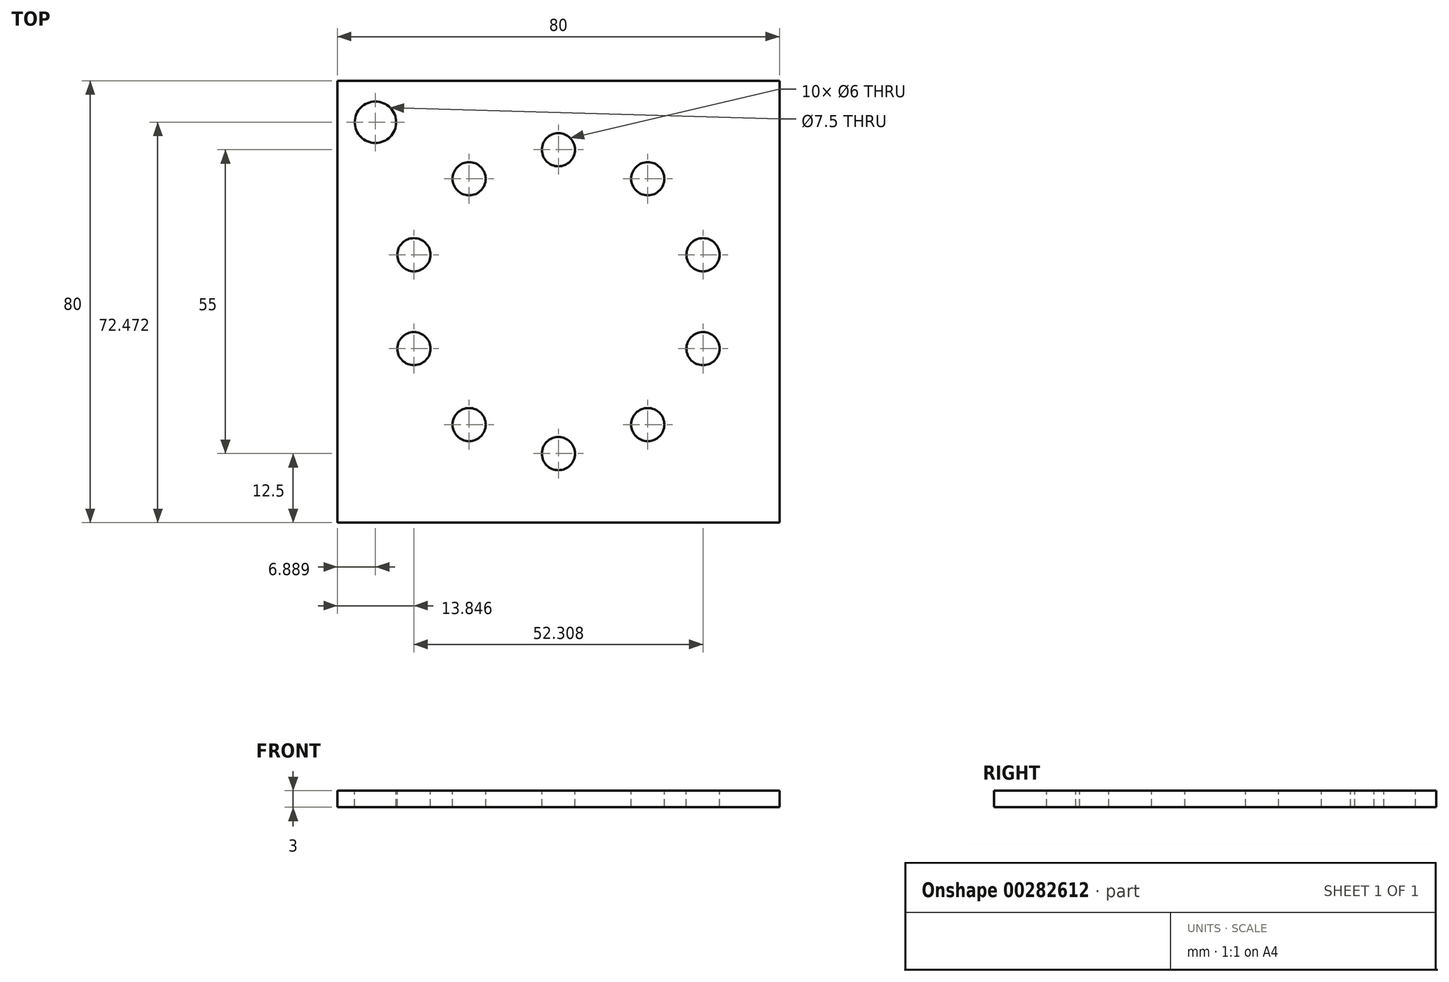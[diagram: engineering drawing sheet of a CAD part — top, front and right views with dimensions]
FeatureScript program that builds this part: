
annotation { "Feature Type Name" : "Feature", "Feature Type Description" : "" }
export const myFeature = defineFeature(function(context is Context, id is Id, definition is map)
    precondition{}
    {
        {
            var Q0;
            Q0=qCreatedBy(makeId("Top.planeOp"),FACE);
            var sketch = newSketch(context, id + "F0", { "sketchPlane" : qUnion([Q0])});
            skLineSegment(sketch, "E0.bottom", {"start": v(-40, 40) * mm, "end": v(40, 40) * mm});
            skLineSegment(sketch, "E0.top", {"start": v(-40, -40) * mm, "end": v(40, -40) * mm});
            skLineSegment(sketch, "E0.left", {"start": v(-40, 40) * mm, "end": v(-40, -40) * mm});
            skLineSegment(sketch, "E0.right", {"start": v(40, 40) * mm, "end": v(40, -40) * mm});
            skPoint(sketch, "E0.middle", {"position": v(0, 0) * mm});
            skSolve(sketch);
        }
        {
            var Q0;
            Q0=makeQuery(id+"F0.imprint","IMPRINT",FACE,{"disambiguationData":[TD([[makeQuery(id+"F0.imprint","IMPRINT",EDGE,{"derivedFrom":sQuery(id+"F0.wireOp",EDGE,"E0.bottom")}),-1.0]])]});
            extrude(context, id + "F1", {"entities" : qUnion([Q0]), "depth" : 3 * mm});
        }
        {
            var Q0;
            Q0=makeQuery(id+"F1.opExtrude","CAP_FACE",FACE,{"disambiguationData":[OSD([sQuery(id+"F0.wireOp",EDGE,"E0.bottom"),sQuery(id+"F0.wireOp",EDGE,"E0.top"),sQuery(id+"F0.wireOp",EDGE,"E0.left"),sQuery(id+"F0.wireOp",EDGE,"E0.right")])],"isStart":false});
            var sketch = newSketch(context, id + "F2", { "sketchPlane" : qUnion([Q0])});
            skCircle(sketch, "E1", {"center": v(0, 0) * mm, "radius": 35 * mm});
            skCircle(sketch, "E2", {"center": v(0, 0) * mm, "radius": 27.5 * mm});
            skCircle(sketch, "E3", {"center": v(0, 27.5) * mm, "radius": 3 * mm});
            skCircle(sketch, "E4.1.0", {"center": v(-16.16, 22.25) * mm, "radius": 3 * mm});
            skCircle(sketch, "E4.2.0", {"center": v(-26.15, 8.5) * mm, "radius": 3 * mm});
            skCircle(sketch, "E4.3.0", {"center": v(-26.15, -8.5) * mm, "radius": 3 * mm});
            skCircle(sketch, "E4.4.0", {"center": v(-16.16, -22.25) * mm, "radius": 3 * mm});
            skCircle(sketch, "E4.5.0", {"center": v(0, -27.5) * mm, "radius": 3 * mm});
            skCircle(sketch, "E4.6.0", {"center": v(16.16, -22.25) * mm, "radius": 3 * mm});
            skCircle(sketch, "E4.7.0", {"center": v(26.15, -8.5) * mm, "radius": 3 * mm});
            skCircle(sketch, "E4.8.0", {"center": v(26.15, 8.5) * mm, "radius": 3 * mm});
            skCircle(sketch, "E4.9.0", {"center": v(16.16, 22.25) * mm, "radius": 3 * mm});
            skSolve(sketch);
        }
        {
            var Q0;
            {var subQ0=sQuery(id+"F2.wireOp",EDGE,"E4.1.0");var subQ1=sQuery(id+"F2.wireOp",EDGE,"E2");var subQ2=makeQuery(id+"F2.imprint","INTERSECT",VERTEX,{"disambiguationData":[OD(0.0)],"derivedFrom":[subQ1,subQ0]});Q0=makeQuery(id+"F2.imprint","IMPRINT",FACE,{"disambiguationData":[TD([[makeQuery(id+"F2.imprint","IMPRINT",EDGE,{"disambiguationData":[TD([[subQ2,-1.0]])],"derivedFrom":subQ1}),1.0]])]});}
            var Q1;
            {var subQ0=sQuery(id+"F2.wireOp",EDGE,"E4.1.0");var subQ1=sQuery(id+"F2.wireOp",EDGE,"E2");var subQ2=makeQuery(id+"F2.imprint","INTERSECT",VERTEX,{"disambiguationData":[OD(0.0)],"derivedFrom":[subQ1,subQ0]});Q1=makeQuery(id+"F2.imprint","IMPRINT",FACE,{"disambiguationData":[TD([[makeQuery(id+"F2.imprint","IMPRINT",EDGE,{"disambiguationData":[TD([[subQ2,-1.0]])],"derivedFrom":subQ1}),-1.0]])]});}
            var Q2;
            {var subQ0=sQuery(id+"F2.wireOp",EDGE,"E3");var subQ1=sQuery(id+"F2.wireOp",EDGE,"E2");var subQ2=makeQuery(id+"F2.imprint","INTERSECT",VERTEX,{"disambiguationData":[OD(0.0)],"derivedFrom":[subQ1,subQ0]});Q2=makeQuery(id+"F2.imprint","IMPRINT",FACE,{"disambiguationData":[TD([[makeQuery(id+"F2.imprint","IMPRINT",EDGE,{"disambiguationData":[TD([[subQ2,-1.0]])],"derivedFrom":subQ1}),1.0]])]});}
            var Q3;
            {var subQ0=sQuery(id+"F2.wireOp",EDGE,"E3");var subQ1=sQuery(id+"F2.wireOp",EDGE,"E2");var subQ2=makeQuery(id+"F2.imprint","INTERSECT",VERTEX,{"disambiguationData":[OD(0.0)],"derivedFrom":[subQ1,subQ0]});Q3=makeQuery(id+"F2.imprint","IMPRINT",FACE,{"disambiguationData":[TD([[makeQuery(id+"F2.imprint","IMPRINT",EDGE,{"disambiguationData":[TD([[subQ2,-1.0]])],"derivedFrom":subQ1}),-1.0]])]});}
            var Q4;
            {var subQ0=sQuery(id+"F2.wireOp",EDGE,"E4.9.0");var subQ1=sQuery(id+"F2.wireOp",EDGE,"E2");var subQ2=makeQuery(id+"F2.imprint","INTERSECT",VERTEX,{"disambiguationData":[OD(0.0)],"derivedFrom":[subQ1,subQ0]});Q4=makeQuery(id+"F2.imprint","IMPRINT",FACE,{"disambiguationData":[TD([[makeQuery(id+"F2.imprint","IMPRINT",EDGE,{"disambiguationData":[TD([[subQ2,-1.0]])],"derivedFrom":subQ1}),1.0]])]});}
            var Q5;
            {var subQ0=sQuery(id+"F2.wireOp",EDGE,"E4.9.0");var subQ1=sQuery(id+"F2.wireOp",EDGE,"E2");var subQ2=makeQuery(id+"F2.imprint","INTERSECT",VERTEX,{"disambiguationData":[OD(0.0)],"derivedFrom":[subQ1,subQ0]});Q5=makeQuery(id+"F2.imprint","IMPRINT",FACE,{"disambiguationData":[TD([[makeQuery(id+"F2.imprint","IMPRINT",EDGE,{"disambiguationData":[TD([[subQ2,-1.0]])],"derivedFrom":subQ1}),-1.0]])]});}
            var Q6;
            {var subQ0=sQuery(id+"F2.wireOp",EDGE,"E4.8.0");var subQ1=sQuery(id+"F2.wireOp",EDGE,"E2");var subQ2=makeQuery(id+"F2.imprint","INTERSECT",VERTEX,{"disambiguationData":[OD(0.0)],"derivedFrom":[subQ1,subQ0]});Q6=makeQuery(id+"F2.imprint","IMPRINT",FACE,{"disambiguationData":[TD([[makeQuery(id+"F2.imprint","IMPRINT",EDGE,{"disambiguationData":[TD([[subQ2,1.0]])],"derivedFrom":subQ1}),-1.0]])]});}
            var Q7;
            {var subQ0=sQuery(id+"F2.wireOp",EDGE,"E4.8.0");var subQ1=sQuery(id+"F2.wireOp",EDGE,"E2");var subQ2=makeQuery(id+"F2.imprint","INTERSECT",VERTEX,{"disambiguationData":[OD(0.0)],"derivedFrom":[subQ1,subQ0]});Q7=makeQuery(id+"F2.imprint","IMPRINT",FACE,{"disambiguationData":[TD([[makeQuery(id+"F2.imprint","IMPRINT",EDGE,{"disambiguationData":[TD([[subQ2,1.0]])],"derivedFrom":subQ1}),1.0]])]});}
            var Q8;
            {var subQ0=sQuery(id+"F2.wireOp",EDGE,"E4.7.0");var subQ1=sQuery(id+"F2.wireOp",EDGE,"E2");var subQ2=makeQuery(id+"F2.imprint","INTERSECT",VERTEX,{"disambiguationData":[OD(0.0)],"derivedFrom":[subQ1,subQ0]});Q8=makeQuery(id+"F2.imprint","IMPRINT",FACE,{"disambiguationData":[TD([[makeQuery(id+"F2.imprint","IMPRINT",EDGE,{"disambiguationData":[TD([[subQ2,-1.0]])],"derivedFrom":subQ1}),-1.0]])]});}
            var Q9;
            {var subQ0=sQuery(id+"F2.wireOp",EDGE,"E4.7.0");var subQ1=sQuery(id+"F2.wireOp",EDGE,"E2");var subQ2=makeQuery(id+"F2.imprint","INTERSECT",VERTEX,{"disambiguationData":[OD(0.0)],"derivedFrom":[subQ1,subQ0]});Q9=makeQuery(id+"F2.imprint","IMPRINT",FACE,{"disambiguationData":[TD([[makeQuery(id+"F2.imprint","IMPRINT",EDGE,{"disambiguationData":[TD([[subQ2,-1.0]])],"derivedFrom":subQ1}),1.0]])]});}
            var Q10;
            {var subQ0=sQuery(id+"F2.wireOp",EDGE,"E4.6.0");var subQ1=sQuery(id+"F2.wireOp",EDGE,"E2");var subQ2=makeQuery(id+"F2.imprint","INTERSECT",VERTEX,{"disambiguationData":[OD(0.0)],"derivedFrom":[subQ1,subQ0]});Q10=makeQuery(id+"F2.imprint","IMPRINT",FACE,{"disambiguationData":[TD([[makeQuery(id+"F2.imprint","IMPRINT",EDGE,{"disambiguationData":[TD([[subQ2,-1.0]])],"derivedFrom":subQ1}),-1.0]])]});}
            var Q11;
            {var subQ0=sQuery(id+"F2.wireOp",EDGE,"E4.6.0");var subQ1=sQuery(id+"F2.wireOp",EDGE,"E2");var subQ2=makeQuery(id+"F2.imprint","INTERSECT",VERTEX,{"disambiguationData":[OD(0.0)],"derivedFrom":[subQ1,subQ0]});Q11=makeQuery(id+"F2.imprint","IMPRINT",FACE,{"disambiguationData":[TD([[makeQuery(id+"F2.imprint","IMPRINT",EDGE,{"disambiguationData":[TD([[subQ2,-1.0]])],"derivedFrom":subQ1}),1.0]])]});}
            var Q12;
            {var subQ0=sQuery(id+"F2.wireOp",EDGE,"E4.5.0");var subQ1=sQuery(id+"F2.wireOp",EDGE,"E2");var subQ2=makeQuery(id+"F2.imprint","INTERSECT",VERTEX,{"disambiguationData":[OD(0.0)],"derivedFrom":[subQ1,subQ0]});Q12=makeQuery(id+"F2.imprint","IMPRINT",FACE,{"disambiguationData":[TD([[makeQuery(id+"F2.imprint","IMPRINT",EDGE,{"disambiguationData":[TD([[subQ2,-1.0]])],"derivedFrom":subQ1}),1.0]])]});}
            var Q13;
            {var subQ0=sQuery(id+"F2.wireOp",EDGE,"E4.5.0");var subQ1=sQuery(id+"F2.wireOp",EDGE,"E2");var subQ2=makeQuery(id+"F2.imprint","INTERSECT",VERTEX,{"disambiguationData":[OD(0.0)],"derivedFrom":[subQ1,subQ0]});Q13=makeQuery(id+"F2.imprint","IMPRINT",FACE,{"disambiguationData":[TD([[makeQuery(id+"F2.imprint","IMPRINT",EDGE,{"disambiguationData":[TD([[subQ2,-1.0]])],"derivedFrom":subQ1}),-1.0]])]});}
            var Q14;
            {var subQ0=sQuery(id+"F2.wireOp",EDGE,"E4.4.0");var subQ1=sQuery(id+"F2.wireOp",EDGE,"E2");var subQ2=makeQuery(id+"F2.imprint","INTERSECT",VERTEX,{"disambiguationData":[OD(0.0)],"derivedFrom":[subQ1,subQ0]});Q14=makeQuery(id+"F2.imprint","IMPRINT",FACE,{"disambiguationData":[TD([[makeQuery(id+"F2.imprint","IMPRINT",EDGE,{"disambiguationData":[TD([[subQ2,-1.0]])],"derivedFrom":subQ1}),-1.0]])]});}
            var Q15;
            {var subQ0=sQuery(id+"F2.wireOp",EDGE,"E4.4.0");var subQ1=sQuery(id+"F2.wireOp",EDGE,"E2");var subQ2=makeQuery(id+"F2.imprint","INTERSECT",VERTEX,{"disambiguationData":[OD(0.0)],"derivedFrom":[subQ1,subQ0]});Q15=makeQuery(id+"F2.imprint","IMPRINT",FACE,{"disambiguationData":[TD([[makeQuery(id+"F2.imprint","IMPRINT",EDGE,{"disambiguationData":[TD([[subQ2,-1.0]])],"derivedFrom":subQ1}),1.0]])]});}
            var Q16;
            {var subQ0=sQuery(id+"F2.wireOp",EDGE,"E4.3.0");var subQ1=sQuery(id+"F2.wireOp",EDGE,"E2");var subQ2=makeQuery(id+"F2.imprint","INTERSECT",VERTEX,{"disambiguationData":[OD(0.0)],"derivedFrom":[subQ1,subQ0]});Q16=makeQuery(id+"F2.imprint","IMPRINT",FACE,{"disambiguationData":[TD([[makeQuery(id+"F2.imprint","IMPRINT",EDGE,{"disambiguationData":[TD([[subQ2,-1.0]])],"derivedFrom":subQ1}),1.0]])]});}
            var Q17;
            {var subQ0=sQuery(id+"F2.wireOp",EDGE,"E4.3.0");var subQ1=sQuery(id+"F2.wireOp",EDGE,"E2");var subQ2=makeQuery(id+"F2.imprint","INTERSECT",VERTEX,{"disambiguationData":[OD(0.0)],"derivedFrom":[subQ1,subQ0]});Q17=makeQuery(id+"F2.imprint","IMPRINT",FACE,{"disambiguationData":[TD([[makeQuery(id+"F2.imprint","IMPRINT",EDGE,{"disambiguationData":[TD([[subQ2,-1.0]])],"derivedFrom":subQ1}),-1.0]])]});}
            var Q18;
            {var subQ0=sQuery(id+"F2.wireOp",EDGE,"E4.2.0");var subQ1=sQuery(id+"F2.wireOp",EDGE,"E2");var subQ2=makeQuery(id+"F2.imprint","INTERSECT",VERTEX,{"disambiguationData":[OD(0.0)],"derivedFrom":[subQ1,subQ0]});Q18=makeQuery(id+"F2.imprint","IMPRINT",FACE,{"disambiguationData":[TD([[makeQuery(id+"F2.imprint","IMPRINT",EDGE,{"disambiguationData":[TD([[subQ2,-1.0]])],"derivedFrom":subQ1}),1.0]])]});}
            var Q19;
            {var subQ0=sQuery(id+"F2.wireOp",EDGE,"E4.2.0");var subQ1=sQuery(id+"F2.wireOp",EDGE,"E2");var subQ2=makeQuery(id+"F2.imprint","INTERSECT",VERTEX,{"disambiguationData":[OD(0.0)],"derivedFrom":[subQ1,subQ0]});Q19=makeQuery(id+"F2.imprint","IMPRINT",FACE,{"disambiguationData":[TD([[makeQuery(id+"F2.imprint","IMPRINT",EDGE,{"disambiguationData":[TD([[subQ2,-1.0]])],"derivedFrom":subQ1}),-1.0]])]});}
            extrude(context, id + "F3", {"entities" : qUnion([Q0, Q1, Q2, Q3, Q4, Q5, Q6, Q7, Q8, Q9, Q10, Q11, Q12, Q13, Q14, Q15, Q16, Q17, Q18, Q19]), "operationType" : NewBodyOperationType.REMOVE, "oppositeDirection" : true, "depth" : 25 * mm});
        }
        {
            var Q0;
            Q0=makeQuery(id+"F1.opExtrude","CAP_FACE",FACE,{"disambiguationData":[OSD([sQuery(id+"F0.wireOp",EDGE,"E0.bottom"),sQuery(id+"F0.wireOp",EDGE,"E0.top"),sQuery(id+"F0.wireOp",EDGE,"E0.left"),sQuery(id+"F0.wireOp",EDGE,"E0.right")])],"isStart":false});
            var sketch = newSketch(context, id + "F4", { "sketchPlane" : qUnion([Q0])});
            skCircle(sketch, "E5", {"center": v(-33.11, 32.47) * mm, "radius": 3.75 * mm});
            skSolve(sketch);
        }
        {
            var Q0;
            Q0=makeQuery(id+"F4.imprint","IMPRINT",FACE,{"disambiguationData":[TD([[makeQuery(id+"F4.imprint","IMPRINT",EDGE,{"derivedFrom":sQuery(id+"F4.wireOp",EDGE,"E5")}),1.0]])]});
            extrude(context, id + "F5", {"entities" : qUnion([Q0]), "operationType" : NewBodyOperationType.REMOVE, "oppositeDirection" : true, "depth" : 25 * mm});
        }
    });
